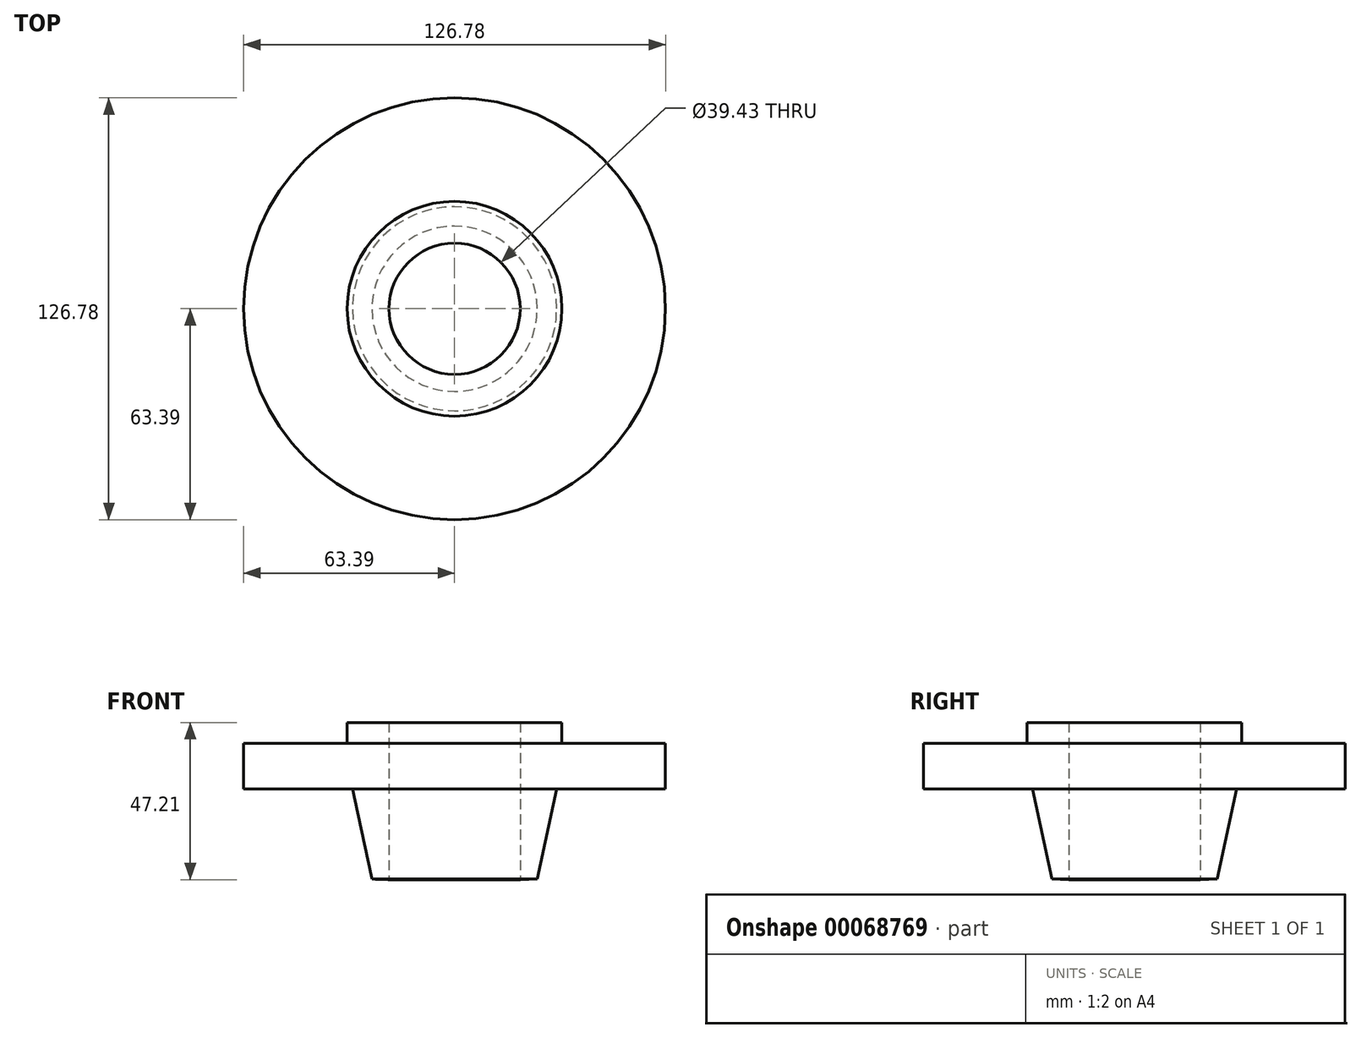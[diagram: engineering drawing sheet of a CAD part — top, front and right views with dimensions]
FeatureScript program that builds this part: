
annotation { "Feature Type Name" : "Feature", "Feature Type Description" : "" }
export const myFeature = defineFeature(function(context is Context, id is Id, definition is map)
    precondition{}
    {
        {
            var Q0;
            Q0=qCreatedBy(makeId("Front.planeOp"),FACE);
            var sketch = newSketch(context, id + "F0", { "sketchPlane" : qUnion([Q0])});
            skLineSegment(sketch, "E0", {"start": v(19.72, 39.34) * mm, "end": v(32.27, 39.34) * mm});
            skLineSegment(sketch, "E1", {"start": v(32.27, 39.34) * mm, "end": v(32.27, 33.15) * mm});
            skLineSegment(sketch, "E2", {"start": v(32.27, 33.15) * mm, "end": v(63.39, 33.15) * mm});
            skLineSegment(sketch, "E3", {"start": v(63.39, 33.15) * mm, "end": v(63.39, 19.36) * mm});
            skLineSegment(sketch, "E4", {"start": v(63.39, 19.36) * mm, "end": v(30.68, 19.36) * mm});
            skLineSegment(sketch, "E5", {"start": v(30.68, 19.36) * mm, "end": v(24.84, -7.7) * mm});
            skLineSegment(sketch, "E6", {"start": v(24.84, -7.7) * mm, "end": v(19.72, -7.87) * mm});
            skLineSegment(sketch, "E7", {"start": v(19.72, -7.87) * mm, "end": v(19.72, 39.34) * mm});
            skPoint(sketch, "E8.orphan", {"position": v(0, 39.34) * mm});
            skLineSegment(sketch, "E9", {"start": v(0, 0) * mm, "end": v(0, 39.34) * mm});
            skSolve(sketch);
        }
        {
            var Q0;
            Q0=makeQuery(id+"F0.imprint","IMPRINT",FACE,{"disambiguationData":[TD([[makeQuery(id+"F0.imprint","IMPRINT",EDGE,{"derivedFrom":sQuery(id+"F0.wireOp",EDGE,"E0")}),-1.0]])]});
            var Q1;
            Q1=sQuery(id+"F0.wireOp",EDGE,"E9");
            revolve(context, id + "F1", {"entities" : qUnion([Q0]), "axis" : qUnion([Q1]), "revolveType" : RevolveType.FULL});
        }
    });
